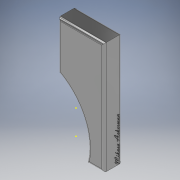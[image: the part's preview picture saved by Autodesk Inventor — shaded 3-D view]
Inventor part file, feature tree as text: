
AUTODESK INVENTOR PART (.ipt)
format: ipt  version: 2021 (Build 250183000, 183)  size: 1,172,992 bytes
history: native  units: mm
features: sketch x8, extrude x5, fillet x4, emboss x1
ambient origin geometry x8: Origin, YZ Plane, XZ Plane, XY Plane, X Axis, Y Axis, Z Axis, Center Point
bodies: Solid1 (feature_tree)
feature tree (18):
  extrude  "Extrusion1"  Depth=18.946mm
  fillet  "Fillet1"  Radius=19.781mm
  sketch  "Sketch2"  dims[d3=7.285mm d4=7.366mm d5=0.0mm d6=1.0mm]
  extrude  "Extrusion2"  Depth=7.366mm TaperAngle=0.0deg
  fillet  "Fillet2"  Radius=1.0mm
  extrude  "Extrusion3"  Depth=1.21mm
  fillet  "Fillet3"  Radius=1.21mm
  sketch  "Sketch5"  dims[d13=0.25mm d14=0.4mm d15=0.8mm]
  extrude  "Extrusion4"  Depth=10.16mm TaperAngle=0.0deg
  extrude  "Extrusion5"  Depth=0.4mm
  fillet  "Fillet4"  Radius=0.8mm
  emboss  "Emboss1"
  sketch  "Sketch1"  dims[d0=46.274mm d1=18.946mm d2=19.781mm]
  sketch  "Sketch3"  dims[d7=1.21mm d8=1.21mm d9=1.21mm]
  sketch  "Sketch4"  dims[d10=1.21mm d11=10.16mm d12=0.0mm]
  sketch  "Sketch6"  dims[d16=1.1mm]
  sketch  "Sketch7"  dims[d17=2.2mm]
  sketch  "Sketch8"  dims[d18=0.8mm d19=1.1mm d20=0.4mm d21=2.2mm d22=10.16mm d23=0.0mm d24=0.15mm d25=2.0mm d26=1.7mm d28=2.0mm d29=0.3mm d30=10.16mm d31=0.0mm d32=0.4mm d33=0.4mm d34=0.4mm d35=0.4mm d36=10.16mm d37=0.0mm d38=0.15mm d39=1.0mm d40=0.0mm]
